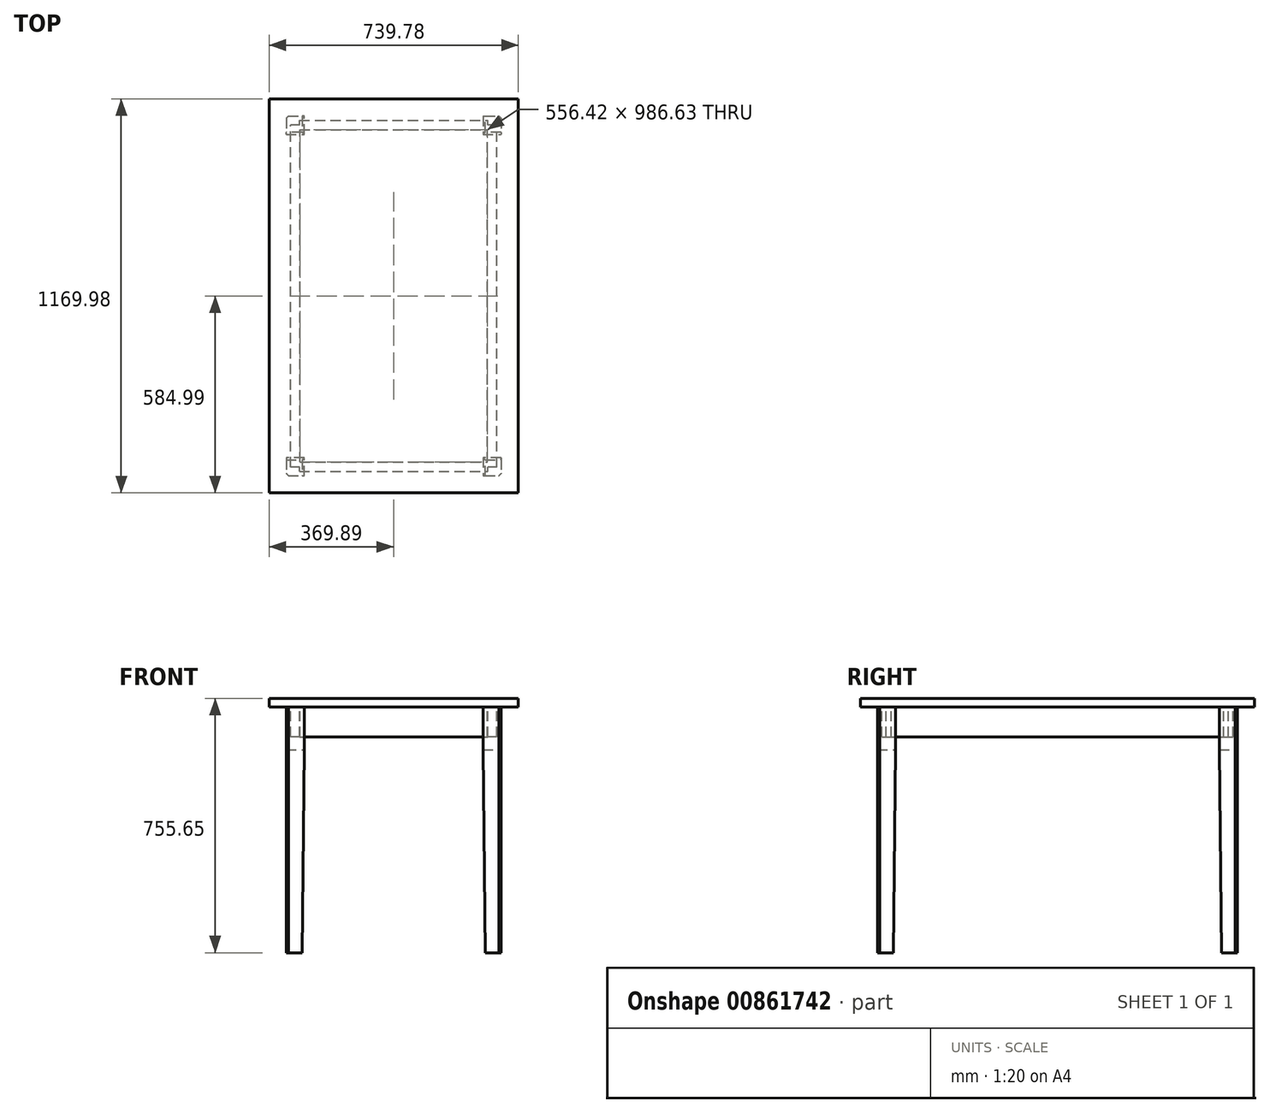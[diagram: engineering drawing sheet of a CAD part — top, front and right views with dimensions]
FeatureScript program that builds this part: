
annotation { "Feature Type Name" : "Feature", "Feature Type Description" : "" }
export const myFeature = defineFeature(function(context is Context, id is Id, definition is map)
    precondition{}
    {
        {
            var Q0;
            Q0=qCreatedBy(makeId("Top.planeOp"),FACE);
            var sketch = newSketch(context, id + "F0", { "sketchPlane" : qUnion([Q0])});
            skLineSegment(sketch, "E0.bottom", {"start": v(-369.89, 585) * mm, "end": v(369.89, 585) * mm});
            skLineSegment(sketch, "E0.top", {"start": v(-369.89, -585) * mm, "end": v(369.89, -585) * mm});
            skLineSegment(sketch, "E0.left", {"start": v(-369.89, 585) * mm, "end": v(-369.89, -585) * mm});
            skLineSegment(sketch, "E0.right", {"start": v(369.89, 585) * mm, "end": v(369.89, -585) * mm});
            skLineSegment(sketch, "E1", {"start": v(-369.89, 585) * mm, "end": v(369.89, -585) * mm, "construction": true});
            skSolve(sketch);
        }
        {
            var Q0;
            Q0 = qSketchRegion(id + "F0", true);
            extrude(context, id + "F1", {"entities" : qUnion([Q0]), "depth" : 25.4 * mm, "offsetDistance" : 25.4 * mm});
        }
        {
            var Q0;
            Q0=makeQuery(id+"F1.opExtrude","CAP_FACE",FACE,{"disambiguationData":[OSD([sQuery(id+"F0.wireOp",EDGE,"E0.bottom"),sQuery(id+"F0.wireOp",EDGE,"E0.top"),sQuery(id+"F0.wireOp",EDGE,"E0.left"),sQuery(id+"F0.wireOp",EDGE,"E0.right")])],"isStart":true});
            var sketch = newSketch(context, id + "F2", { "sketchPlane" : qUnion([Q0])});
            skLineSegment(sketch, "E2.bottom", {"start": v(-292.1, -507.2) * mm, "end": v(292.1, -507.2) * mm, "construction": true});
            skLineSegment(sketch, "E2.top", {"start": v(-292.1, 507.2) * mm, "end": v(292.1, 507.2) * mm, "construction": true});
            skLineSegment(sketch, "E2.left", {"start": v(-292.1, -507.2) * mm, "end": v(-292.1, 507.2) * mm, "construction": true});
            skLineSegment(sketch, "E2.right", {"start": v(292.1, -507.2) * mm, "end": v(292.1, 507.2) * mm, "construction": true});
            skPoint(sketch, "E2.middle", {"position": v(0, 0) * mm});
            skLineSegment(sketch, "E3.bottom", {"start": v(-319.09, -534.2) * mm, "end": v(-265.11, -534.2) * mm});
            skLineSegment(sketch, "E3.top", {"start": v(-319.09, -480.22) * mm, "end": v(-265.11, -480.22) * mm});
            skLineSegment(sketch, "E3.left", {"start": v(-319.09, -534.2) * mm, "end": v(-319.09, -480.22) * mm});
            skLineSegment(sketch, "E3.right", {"start": v(-265.11, -534.2) * mm, "end": v(-265.11, -480.22) * mm});
            skPoint(sketch, "E3.middle", {"position": v(-292.1, -507.2) * mm});
            skLineSegment(sketch, "E4.bottom", {"start": v(265.11, -534.2) * mm, "end": v(319.09, -534.2) * mm});
            skLineSegment(sketch, "E4.top", {"start": v(265.11, -480.22) * mm, "end": v(319.09, -480.22) * mm});
            skLineSegment(sketch, "E4.left", {"start": v(265.11, -534.2) * mm, "end": v(265.11, -480.22) * mm});
            skLineSegment(sketch, "E4.right", {"start": v(319.09, -534.2) * mm, "end": v(319.09, -480.22) * mm});
            skPoint(sketch, "E4.middle", {"position": v(292.1, -507.2) * mm});
            skLineSegment(sketch, "E5.bottom", {"start": v(-319.09, 480.22) * mm, "end": v(-265.11, 480.22) * mm});
            skLineSegment(sketch, "E5.top", {"start": v(-319.09, 534.2) * mm, "end": v(-265.11, 534.2) * mm});
            skLineSegment(sketch, "E5.left", {"start": v(-319.09, 480.22) * mm, "end": v(-319.09, 534.2) * mm});
            skLineSegment(sketch, "E5.right", {"start": v(-265.11, 480.22) * mm, "end": v(-265.11, 534.2) * mm});
            skPoint(sketch, "E5.middle", {"position": v(-292.1, 507.2) * mm});
            skLineSegment(sketch, "E6.bottom", {"start": v(265.11, 480.22) * mm, "end": v(319.09, 480.22) * mm});
            skLineSegment(sketch, "E6.top", {"start": v(265.11, 534.2) * mm, "end": v(319.09, 534.2) * mm});
            skLineSegment(sketch, "E6.left", {"start": v(265.11, 480.22) * mm, "end": v(265.11, 534.2) * mm});
            skLineSegment(sketch, "E6.right", {"start": v(319.09, 480.22) * mm, "end": v(319.09, 534.2) * mm});
            skPoint(sketch, "E6.middle", {"position": v(292.1, 507.2) * mm});
            skSolve(sketch);
        }
        {
            var Q0;
            Q0 = qSketchRegion(id + "F2", true);
            extrude(context, id + "F3", {"entities" : qUnion([Q0]), "depth" : 730.25 * mm, "offsetDistance" : 25.4 * mm});
        }
        {
            var Q0;
            Q0=makeQuery(id+"F2.imprint","IMPRINT",FACE,{"disambiguationData":[TD([[makeQuery(id+"F2.imprint","IMPRINT",EDGE,{"derivedFrom":sQuery(id+"F2.wireOp",EDGE,"E3.bottom")}),-1.0]])]});
            var sketch = newSketch(context, id + "F4", { "sketchPlane" : qUnion([Q0])});
            skLineSegment(sketch, "E7.bottom", {"start": v(-279.4, -493.32) * mm, "end": v(279.4, -493.32) * mm});
            skLineSegment(sketch, "E7.top", {"start": v(-279.4, -521.1) * mm, "end": v(279.4, -521.1) * mm});
            skLineSegment(sketch, "E7.left", {"start": v(-279.4, -493.32) * mm, "end": v(-279.4, -521.1) * mm});
            skLineSegment(sketch, "E7.right", {"start": v(279.4, -493.32) * mm, "end": v(279.4, -521.1) * mm});
            skPoint(sketch, "E7.middle", {"position": v(0, -507.2) * mm});
            skLineSegment(sketch, "E8.bottom", {"start": v(-278.2, 508) * mm, "end": v(-306, 508) * mm});
            skLineSegment(sketch, "E8.top", {"start": v(-278.2, -508) * mm, "end": v(-306, -508) * mm});
            skLineSegment(sketch, "E8.left", {"start": v(-278.2, 508) * mm, "end": v(-278.2, -508) * mm});
            skLineSegment(sketch, "E8.right", {"start": v(-306, 508) * mm, "end": v(-306, -508) * mm});
            skPoint(sketch, "E8.middle", {"position": v(-292.1, 0) * mm});
            skLineSegment(sketch, "E9.bottom", {"start": v(-279.4, 521.1) * mm, "end": v(279.4, 521.1) * mm});
            skLineSegment(sketch, "E9.top", {"start": v(-279.4, 493.32) * mm, "end": v(279.4, 493.32) * mm});
            skLineSegment(sketch, "E9.left", {"start": v(-279.4, 521.1) * mm, "end": v(-279.4, 493.32) * mm});
            skLineSegment(sketch, "E9.right", {"start": v(279.4, 521.1) * mm, "end": v(279.4, 493.32) * mm});
            skPoint(sketch, "E9.middle", {"position": v(0, 507.2) * mm});
            skLineSegment(sketch, "E10.bottom", {"start": v(306, 508) * mm, "end": v(278.2, 508) * mm});
            skLineSegment(sketch, "E10.top", {"start": v(306, -508) * mm, "end": v(278.2, -508) * mm});
            skLineSegment(sketch, "E10.left", {"start": v(306, 508) * mm, "end": v(306, -508) * mm});
            skLineSegment(sketch, "E10.right", {"start": v(278.2, 508) * mm, "end": v(278.2, -508) * mm});
            skPoint(sketch, "E10.middle", {"position": v(292.1, 0) * mm});
            skSolve(sketch);
        }
        {
            var Q0;
            Q0 = qSketchRegion(id + "F4", true);
            extrude(context, id + "F5", {"entities" : qUnion([Q0]), "depth" : 88.9 * mm, "offsetDistance" : 25.4 * mm});
        }
        {
            var Q0;
            Q0=makeQuery(id+"F3.opExtrude","CAP_EDGE",EDGE,{"disambiguationData":[OSD([sQuery(id+"F2.wireOp",EDGE,"E3.right")])],"isStart":false});
            var Q1;
            Q1=makeQuery(id+"F3.opExtrude","CAP_EDGE",EDGE,{"disambiguationData":[OSD([sQuery(id+"F2.wireOp",EDGE,"E3.top")])],"isStart":false});
            chamfer(context, id + "F6", {"entities" : qUnion([Q0, Q1]), "chamferType" : ChamferType.TWO_OFFSETS, "width1" : 6.35 * mm, "oppositeDirection" : false, "width2" : 603.25 * mm, "tangentPropagation" : true});
        }
        {
            var Q0;
            Q0=makeQuery(id+"F3.opExtrude","CAP_EDGE",EDGE,{"disambiguationData":[OSD([sQuery(id+"F2.wireOp",EDGE,"E4.left")])],"isStart":false});
            var Q1;
            Q1=makeQuery(id+"F3.opExtrude","CAP_EDGE",EDGE,{"disambiguationData":[OSD([sQuery(id+"F2.wireOp",EDGE,"E4.top")])],"isStart":false});
            chamfer(context, id + "F7", {"entities" : qUnion([Q0, Q1]), "chamferType" : ChamferType.TWO_OFFSETS, "width1" : 6.35 * mm, "oppositeDirection" : true, "width2" : 603.25 * mm, "tangentPropagation" : true});
        }
        {
            var Q0;
            Q0=makeQuery(id+"F3.opExtrude","CAP_EDGE",EDGE,{"disambiguationData":[OSD([sQuery(id+"F2.wireOp",EDGE,"E6.bottom")])],"isStart":false});
            var Q1;
            Q1=makeQuery(id+"F3.opExtrude","CAP_EDGE",EDGE,{"disambiguationData":[OSD([sQuery(id+"F2.wireOp",EDGE,"E6.left")])],"isStart":false});
            chamfer(context, id + "F8", {"entities" : qUnion([Q0, Q1]), "chamferType" : ChamferType.TWO_OFFSETS, "width1" : 6.35 * mm, "oppositeDirection" : false, "width2" : 603.25 * mm, "tangentPropagation" : true});
        }
        {
            var Q0;
            Q0=makeQuery(id+"F3.opExtrude","CAP_EDGE",EDGE,{"disambiguationData":[OSD([sQuery(id+"F2.wireOp",EDGE,"E5.right")])],"isStart":false});
            var Q1;
            Q1=makeQuery(id+"F3.opExtrude","CAP_EDGE",EDGE,{"disambiguationData":[OSD([sQuery(id+"F2.wireOp",EDGE,"E5.bottom")])],"isStart":false});
            chamfer(context, id + "F9", {"entities" : qUnion([Q0, Q1]), "chamferType" : ChamferType.TWO_OFFSETS, "width1" : 6.35 * mm, "oppositeDirection" : false, "width2" : 603.25 * mm, "tangentPropagation" : true});
        }
        {
            var Q0;
            Q0=makeQuery(id+"F3.opExtrude","SWEPT_EDGE",EDGE,{"disambiguationData":[OSD([sQuery(id+"F2.wireOp",EDGE,"E5.top"),sQuery(id+"F2.wireOp",EDGE,"E5.left")])]});
            chamfer(context, id + "F10", {"entities" : qUnion([Q0]), "width" : 6.35 * mm, "tangentPropagation" : true});
        }
        {
            var Q0;
            Q0=makeQuery(id+"F3.opExtrude","SWEPT_EDGE",EDGE,{"disambiguationData":[OSD([sQuery(id+"F2.wireOp",EDGE,"E6.top"),sQuery(id+"F2.wireOp",EDGE,"E6.right")])]});
            chamfer(context, id + "F11", {"entities" : qUnion([Q0]), "width" : 6.35 * mm, "tangentPropagation" : true});
        }
        {
            var Q0;
            Q0=makeQuery(id+"F3.opExtrude","SWEPT_EDGE",EDGE,{"disambiguationData":[OSD([sQuery(id+"F2.wireOp",EDGE,"E3.bottom"),sQuery(id+"F2.wireOp",EDGE,"E3.left")])]});
            chamfer(context, id + "F12", {"entities" : qUnion([Q0]), "width" : 6.35 * mm, "tangentPropagation" : true});
        }
        {
            var Q0;
            Q0=makeQuery(id+"F3.opExtrude","SWEPT_EDGE",EDGE,{"disambiguationData":[OSD([sQuery(id+"F2.wireOp",EDGE,"E4.bottom"),sQuery(id+"F2.wireOp",EDGE,"E4.right")])]});
            chamfer(context, id + "F13", {"entities" : qUnion([Q0]), "width" : 6.35 * mm, "tangentPropagation" : true});
        }
    });
